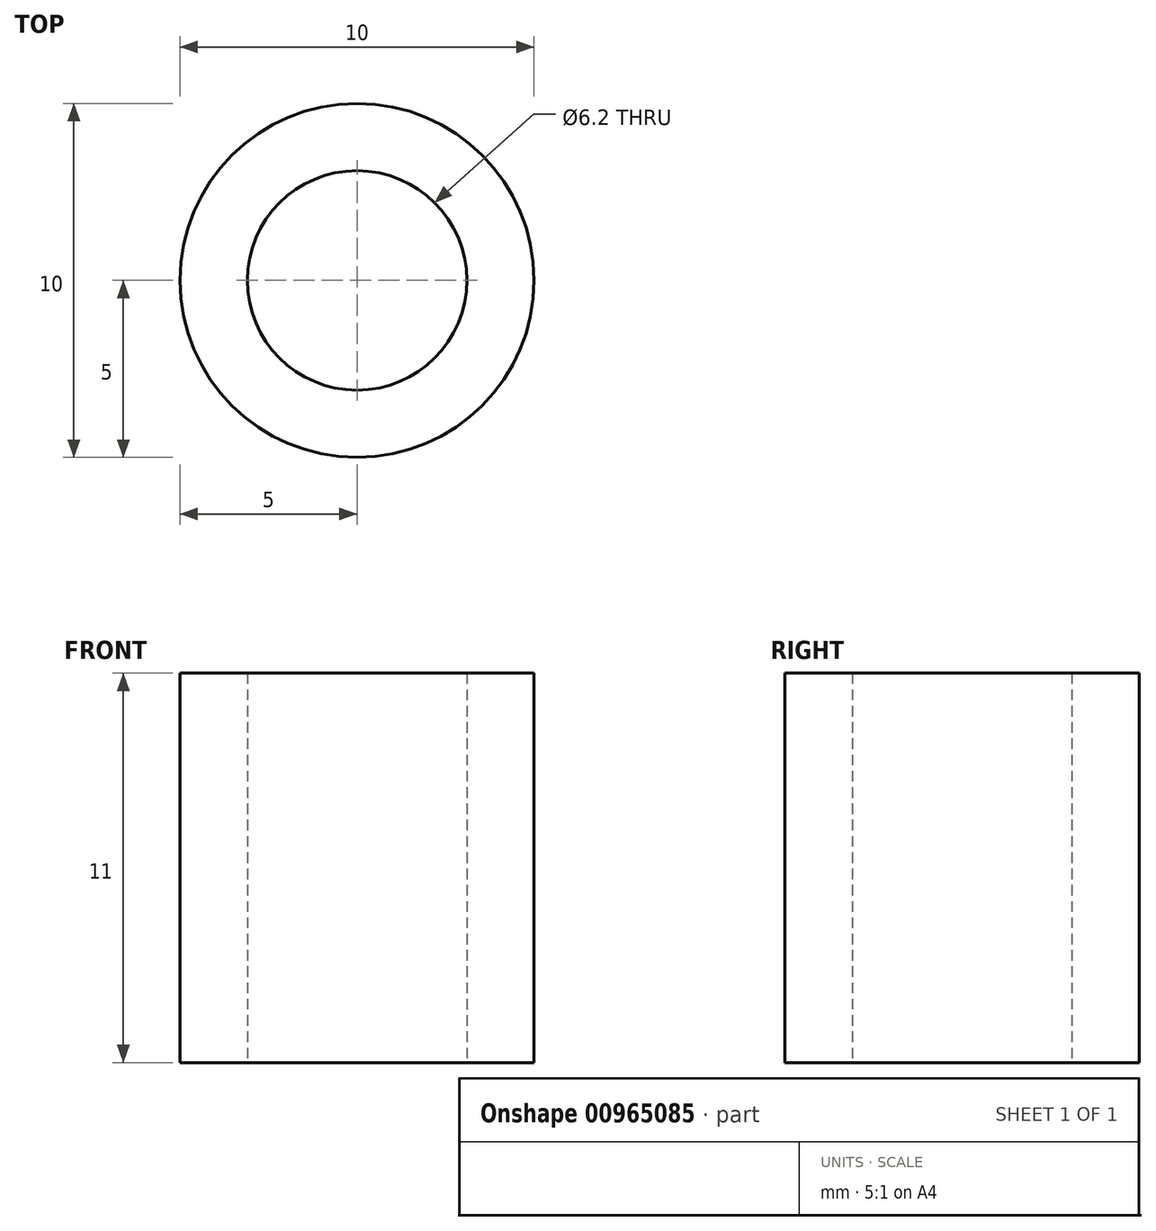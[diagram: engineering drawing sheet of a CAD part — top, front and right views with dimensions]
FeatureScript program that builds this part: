
annotation { "Feature Type Name" : "Feature", "Feature Type Description" : "" }
export const myFeature = defineFeature(function(context is Context, id is Id, definition is map)
    precondition{}
    {
        {
            var Q0;
            Q0=qCreatedBy(makeId("Top.planeOp"),FACE);
            var sketch = newSketch(context, id + "F0", { "sketchPlane" : qUnion([Q0])});
            skCircle(sketch, "E0", {"center": v(0, 0) * mm, "radius": 3.1 * mm});
            skCircle(sketch, "E1", {"center": v(0, 0) * mm, "radius": 5 * mm});
            skSolve(sketch);
        }
        {
            var Q0;
            Q0=makeQuery(id+"F0.imprint","IMPRINT",FACE,{"disambiguationData":[TD([[makeQuery(id+"F0.imprint","IMPRINT",EDGE,{"derivedFrom":sQuery(id+"F0.wireOp",EDGE,"E0")}),-1.0]])]});
            extrude(context, id + "F1", {"entities" : qUnion([Q0]), "depth" : 11 * mm, "offsetDistance" : 25 * mm});
        }
    });
